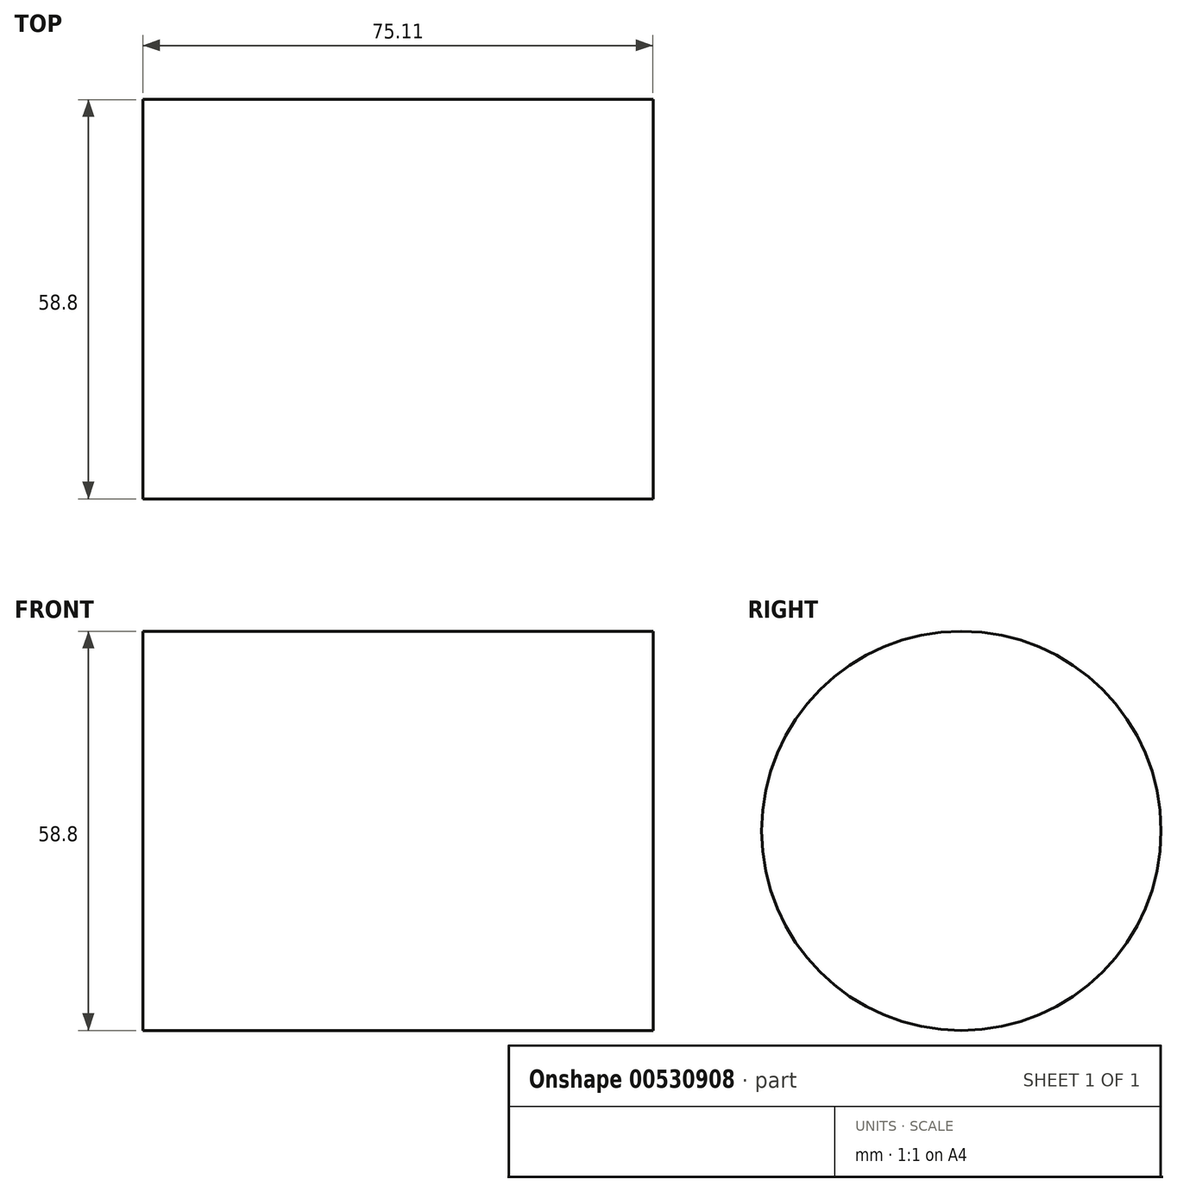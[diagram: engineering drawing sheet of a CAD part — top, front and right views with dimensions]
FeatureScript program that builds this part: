
annotation { "Feature Type Name" : "Feature", "Feature Type Description" : "" }
export const myFeature = defineFeature(function(context is Context, id is Id, definition is map)
    precondition{}
    {
        {
            var Q0;
            Q0=qCreatedBy(makeId("Front.planeOp"),FACE);
            var sketch = newSketch(context, id + "F0", { "sketchPlane" : qUnion([Q0])});
            skLineSegment(sketch, "E0.bottom", {"start": v(0, 29.4) * mm, "end": v(75.11, 29.4) * mm});
            skLineSegment(sketch, "E0.top", {"start": v(0, 0) * mm, "end": v(75.11, 0) * mm});
            skLineSegment(sketch, "E0.left", {"start": v(0, 29.4) * mm, "end": v(0, 0) * mm});
            skLineSegment(sketch, "E0.right", {"start": v(75.11, 29.4) * mm, "end": v(75.11, 0) * mm});
            skLineSegment(sketch, "E1", {"start": v(-72.2, 0) * mm, "end": v(75.11, 0) * mm, "construction": true});
            skSolve(sketch);
        }
        {
            var Q0;
            Q0=makeQuery(id+"F0.imprint","IMPRINT",FACE,{"disambiguationData":[TD([[makeQuery(id+"F0.imprint","IMPRINT",EDGE,{"derivedFrom":sQuery(id+"F0.wireOp",EDGE,"E0.bottom")}),-1.0]])]});
            var Q1;
            Q1=sQuery(id+"F0.wireOp",EDGE,"E1");
            revolve(context, id + "F1", {"entities" : qUnion([Q0]), "axis" : qUnion([Q1]), "revolveType" : RevolveType.FULL});
        }
    });
